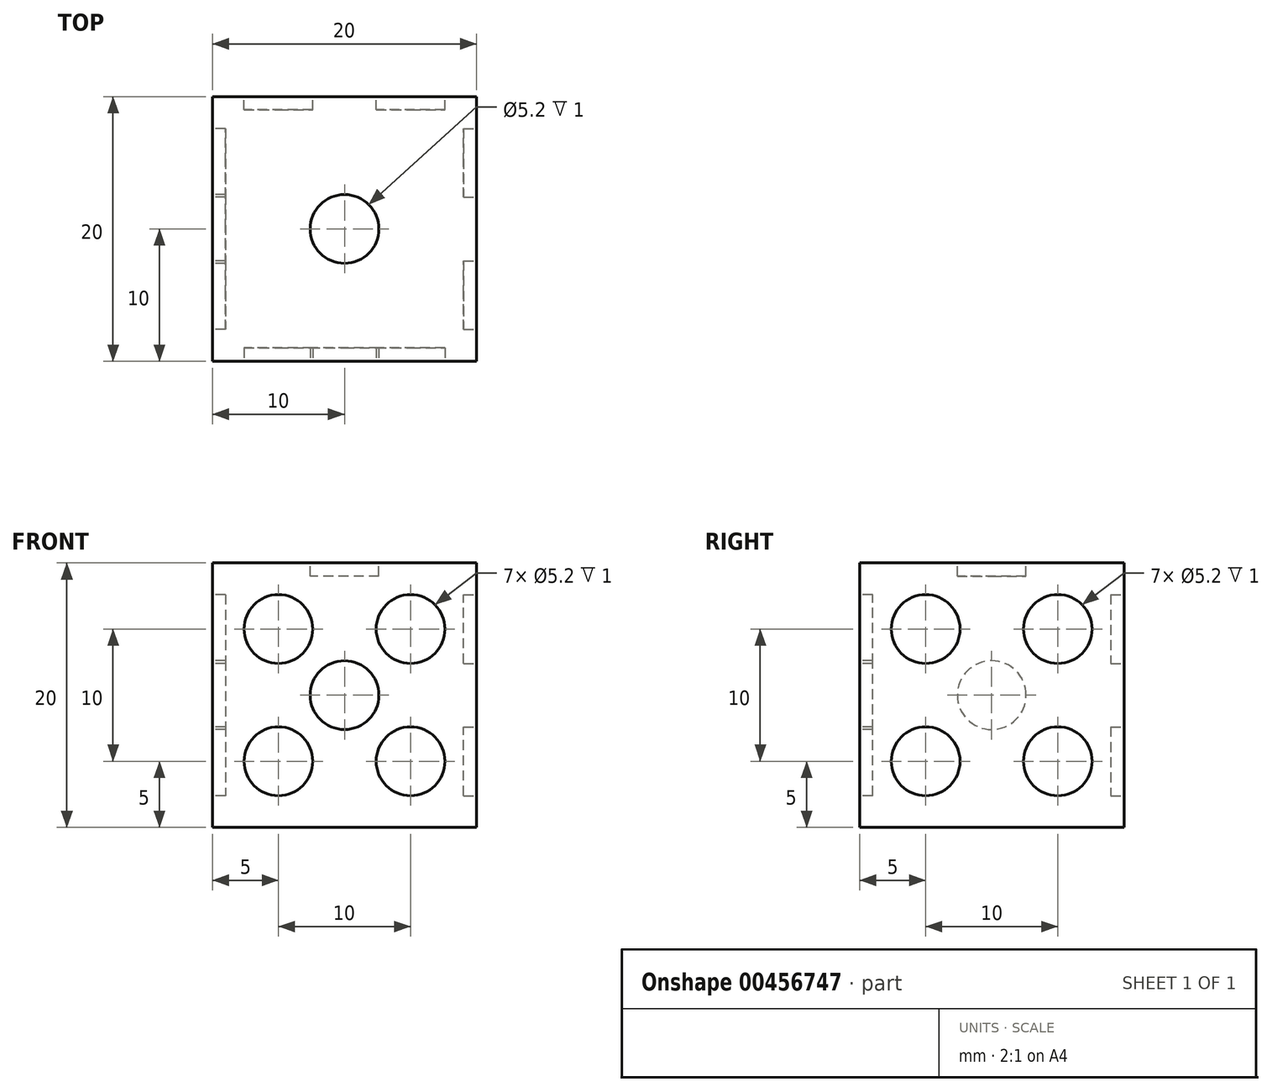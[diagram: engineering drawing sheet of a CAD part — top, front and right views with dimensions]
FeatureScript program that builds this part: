
annotation { "Feature Type Name" : "Feature", "Feature Type Description" : "" }
export const myFeature = defineFeature(function(context is Context, id is Id, definition is map)
    precondition{}
    {
        {
            var Q0;
            Q0=qCreatedBy(makeId("Front.planeOp"),FACE);
            var sketch = newSketch(context, id + "F0", { "sketchPlane" : qUnion([Q0])});
            skLineSegment(sketch, "E0.bottom", {"start": v(0, 0) * mm, "end": v(-20, 0) * mm});
            skLineSegment(sketch, "E0.top", {"start": v(0, 20) * mm, "end": v(-20, 20) * mm});
            skLineSegment(sketch, "E0.left", {"start": v(0, 0) * mm, "end": v(0, 20) * mm});
            skLineSegment(sketch, "E0.right", {"start": v(-20, 0) * mm, "end": v(-20, 20) * mm});
            skSolve(sketch);
        }
        {
            var Q0;
            Q0=makeQuery(id+"F0.imprint","IMPRINT",FACE,{"disambiguationData":[TD([[makeQuery(id+"F0.imprint","IMPRINT",EDGE,{"derivedFrom":sQuery(id+"F0.wireOp",EDGE,"E0.bottom")}),-1.0]])]});
            extrude(context, id + "F1", {"entities" : qUnion([Q0]), "depth" : 20 * mm});
        }
        {
            var Q0;
            Q0=makeQuery(id+"F1.opExtrude","CAP_FACE",FACE,{"disambiguationData":[OSD([sQuery(id+"F0.wireOp",EDGE,"E0.bottom"),sQuery(id+"F0.wireOp",EDGE,"E0.top"),sQuery(id+"F0.wireOp",EDGE,"E0.left"),sQuery(id+"F0.wireOp",EDGE,"E0.right")])],"isStart":false});
            var sketch = newSketch(context, id + "F2", { "sketchPlane" : qUnion([Q0])});
            skLineSegment(sketch, "E1", {"start": v(-10, 20) * mm, "end": v(-10, 0) * mm, "construction": true});
            skLineSegment(sketch, "E2", {"start": v(-20, 20) * mm, "end": v(0, 0) * mm, "construction": true});
            skLineSegment(sketch, "E3", {"start": v(0, 20) * mm, "end": v(-20, 0) * mm, "construction": true});
            skLineSegment(sketch, "E4", {"start": v(-20, 10) * mm, "end": v(0, 10) * mm, "construction": true});
            skCircle(sketch, "E5", {"center": v(-15, 15) * mm, "radius": 2.6 * mm});
            skCircle(sketch, "E6", {"center": v(-10, 10) * mm, "radius": 2.6 * mm});
            skCircle(sketch, "E7", {"center": v(-15, 5) * mm, "radius": 2.6 * mm});
            skCircle(sketch, "E8", {"center": v(-5, 15) * mm, "radius": 2.6 * mm});
            skCircle(sketch, "E9", {"center": v(-5, 5) * mm, "radius": 2.6 * mm});
            skSolve(sketch);
        }
        {
            var Q0;
            Q0=qSketchRegion(id+"F2",true);
            extrude(context, id + "F3", {"entities" : qUnion([Q0]), "operationType" : NewBodyOperationType.REMOVE, "oppositeDirection" : true, "depth" : 1 * mm});
        }
        {
            var Q0;
            Q0=makeQuery(id+"F1.opExtrude","CAP_FACE",FACE,{"disambiguationData":[OSD([sQuery(id+"F0.wireOp",EDGE,"E0.bottom"),sQuery(id+"F0.wireOp",EDGE,"E0.top"),sQuery(id+"F0.wireOp",EDGE,"E0.left"),sQuery(id+"F0.wireOp",EDGE,"E0.right")])],"isStart":true});
            var sketch = newSketch(context, id + "F4", { "sketchPlane" : qUnion([Q0])});
            skLineSegment(sketch, "E10", {"start": v(20, 20) * mm, "end": v(0, 0) * mm, "construction": true});
            skCircle(sketch, "E11", {"center": v(15, 15) * mm, "radius": 2.6 * mm});
            skCircle(sketch, "E12", {"center": v(5, 5) * mm, "radius": 2.6 * mm});
            skSolve(sketch);
        }
        {
            var Q0;
            Q0=qSketchRegion(id+"F4",true);
            extrude(context, id + "F5", {"entities" : qUnion([Q0]), "operationType" : NewBodyOperationType.REMOVE, "oppositeDirection" : true, "depth" : 1 * mm});
        }
        {
            var Q0;
            Q0=makeQuery(id+"F1.opExtrude","SWEPT_FACE",FACE,{"disambiguationData":[OSD([sQuery(id+"F0.wireOp",EDGE,"E0.top")])]});
            var sketch = newSketch(context, id + "F6", { "sketchPlane" : qUnion([Q0])});
            skLineSegment(sketch, "E13", {"start": v(-10, 0) * mm, "end": v(-10, -20) * mm, "construction": true});
            skLineSegment(sketch, "E14", {"start": v(-20, -10) * mm, "end": v(0, -10) * mm, "construction": true});
            skCircle(sketch, "E15", {"center": v(-10, -10) * mm, "radius": 2.6 * mm});
            skSolve(sketch);
        }
        {
            var Q0;
            Q0=qSketchRegion(id+"F6",true);
            extrude(context, id + "F7", {"entities" : qUnion([Q0]), "operationType" : NewBodyOperationType.REMOVE, "oppositeDirection" : true, "depth" : 1 * mm});
        }
        {
            var Q0;
            Q0=makeQuery(id+"F1.opExtrude","SWEPT_FACE",FACE,{"disambiguationData":[OSD([sQuery(id+"F0.wireOp",EDGE,"E0.right")])]});
            var sketch = newSketch(context, id + "F8", { "sketchPlane" : qUnion([Q0])});
            skLineSegment(sketch, "E16", {"start": v(20, 20) * mm, "end": v(0, 0) * mm, "construction": true});
            skCircle(sketch, "E17", {"center": v(10, 10) * mm, "radius": 2.6 * mm});
            skCircle(sketch, "E18", {"center": v(15, 15) * mm, "radius": 2.6 * mm});
            skCircle(sketch, "E19", {"center": v(5, 5) * mm, "radius": 2.6 * mm});
            skSolve(sketch);
        }
        {
            var Q0;
            Q0=qSketchRegion(id+"F8",true);
            extrude(context, id + "F9", {"entities" : qUnion([Q0]), "operationType" : NewBodyOperationType.REMOVE, "oppositeDirection" : true, "depth" : 1 * mm});
        }
        {
            var Q0;
            Q0=makeQuery(id+"F1.opExtrude","SWEPT_FACE",FACE,{"disambiguationData":[OSD([sQuery(id+"F0.wireOp",EDGE,"E0.left")])]});
            var sketch = newSketch(context, id + "F10", { "sketchPlane" : qUnion([Q0])});
            skLineSegment(sketch, "E20", {"start": v(-20, 20) * mm, "end": v(0, 0) * mm, "construction": true});
            skLineSegment(sketch, "E21", {"start": v(0, 20) * mm, "end": v(-20, 0) * mm, "construction": true});
            skLineSegment(sketch, "E22", {"start": v(-20, 10) * mm, "end": v(0, 10) * mm, "construction": true});
            skLineSegment(sketch, "E23", {"start": v(-10, 20) * mm, "end": v(-10, 0) * mm, "construction": true});
            skCircle(sketch, "E24", {"center": v(-15, 15) * mm, "radius": 2.6 * mm});
            skCircle(sketch, "E25", {"center": v(-15, 5) * mm, "radius": 2.6 * mm});
            skCircle(sketch, "E26", {"center": v(-5, 15) * mm, "radius": 2.6 * mm});
            skCircle(sketch, "E27", {"center": v(-5, 5) * mm, "radius": 2.6 * mm});
            skSolve(sketch);
        }
        {
            var Q0;
            Q0=qSketchRegion(id+"F10",true);
            extrude(context, id + "F11", {"entities" : qUnion([Q0]), "operationType" : NewBodyOperationType.REMOVE, "oppositeDirection" : true, "depth" : 1 * mm});
        }
    });
